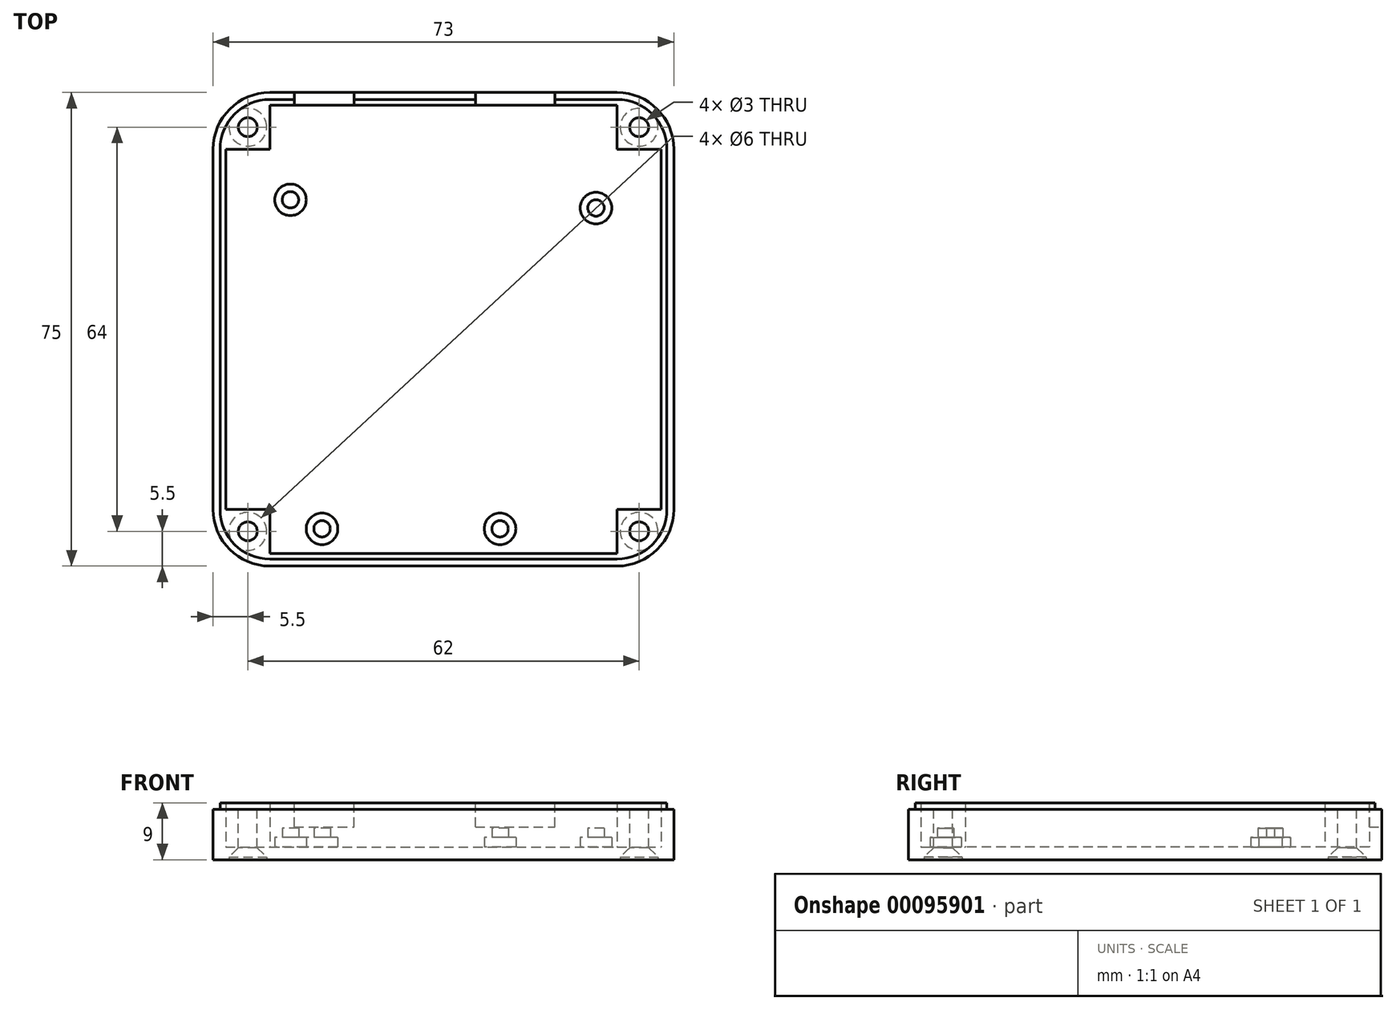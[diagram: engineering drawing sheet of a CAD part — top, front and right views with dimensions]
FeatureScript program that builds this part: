
annotation { "Feature Type Name" : "Feature", "Feature Type Description" : "" }
export const myFeature = defineFeature(function(context is Context, id is Id, definition is map)
    precondition{}
    {
        {
            var Q0;
            Q0=qCreatedBy(makeId("Top.planeOp"),FACE);
            var sketch = newSketch(context, id + "F0", { "sketchPlane" : qUnion([Q0])});
            skLineSegment(sketch, "E0.bottom", {"start": v(-27.5, 38.5) * mm, "end": v(27.5, 38.5) * mm});
            skLineSegment(sketch, "E0.top", {"start": v(-27.5, -36.5) * mm, "end": v(27.5, -36.5) * mm});
            skLineSegment(sketch, "E0.left", {"start": v(-36.5, 29.5) * mm, "end": v(-36.5, -27.5) * mm});
            skLineSegment(sketch, "E0.right", {"start": v(36.5, 29.5) * mm, "end": v(36.5, -27.5) * mm});
            skPoint(sketch, "E1.visualSharp", {"position": v(-36.5, 38.5) * mm});
            skArc(sketch, "E1.filletArc", {"start": v(-27.5, 38.5) * mm, "mid": v(-33.86, 35.86) * mm, "end": v(-36.5, 29.5) * mm});
            skPoint(sketch, "E2.visualSharp", {"position": v(36.5, 38.5) * mm});
            skArc(sketch, "E2.filletArc", {"start": v(36.5, 29.5) * mm, "mid": v(33.86, 35.86) * mm, "end": v(27.5, 38.5) * mm});
            skPoint(sketch, "E3.visualSharp", {"position": v(36.5, -36.5) * mm});
            skArc(sketch, "E3.filletArc", {"start": v(27.5, -36.5) * mm, "mid": v(33.86, -33.86) * mm, "end": v(36.5, -27.5) * mm});
            skPoint(sketch, "E4.visualSharp", {"position": v(-36.5, -36.5) * mm});
            skArc(sketch, "E4.filletArc", {"start": v(-36.5, -27.5) * mm, "mid": v(-33.86, -33.86) * mm, "end": v(-27.5, -36.5) * mm});
            skSolve(sketch);
        }
        {
            var Q0;
            Q0=qSketchRegion(id+"F0",true);
            extrude(context, id + "F1", {"entities" : qUnion([Q0]), "depth" : 2 * mm});
        }
        {
            var Q0;
            Q0=makeQuery(id+"F1.opExtrude","CAP_FACE",FACE,{"disambiguationData":[OSD([sQuery(id+"F0.wireOp",EDGE,"E0.bottom"),sQuery(id+"F0.wireOp",EDGE,"E0.top"),sQuery(id+"F0.wireOp",EDGE,"E0.left"),sQuery(id+"F0.wireOp",EDGE,"E0.right")])],"isStart":false});
            var sketch = newSketch(context, id + "F2", { "sketchPlane" : qUnion([Q0])});
            skCircle(sketch, "E5", {"center": v(-19.24, -30.6) * mm, "radius": 2.5 * mm});
            skCircle(sketch, "E6", {"center": v(8.96, -30.6) * mm, "radius": 2.5 * mm});
            skCircle(sketch, "E7", {"center": v(24.16, 20.2) * mm, "radius": 2.5 * mm});
            skCircle(sketch, "E8", {"center": v(-24.24, 21.5) * mm, "radius": 2.5 * mm});
            skSolve(sketch);
        }
        {
            var Q0;
            Q0=qSketchRegion(id+"F2",true);
            extrude(context, id + "F3", {"entities" : qUnion([Q0]), "operationType" : NewBodyOperationType.ADD, "depth" : 1.5 * mm});
        }
        {
            var Q0;
            Q0=makeQuery(id+"F3.opExtrude","CAP_FACE",FACE,{"disambiguationData":[OSD([sQuery(id+"F2.wireOp",EDGE,"E8")])],"isStart":false});
            var sketch = newSketch(context, id + "F4", { "sketchPlane" : qUnion([Q0])});
            skCircle(sketch, "E9", {"center": v(-19.24, -30.6) * mm, "radius": 1.3 * mm});
            skCircle(sketch, "E10", {"center": v(8.96, -30.6) * mm, "radius": 1.3 * mm});
            skCircle(sketch, "E11", {"center": v(24.16, 20.2) * mm, "radius": 1.3 * mm});
            skCircle(sketch, "E12", {"center": v(-24.24, 21.5) * mm, "radius": 1.3 * mm});
            skSolve(sketch);
        }
        {
            var Q0;
            Q0=qSketchRegion(id+"F4",true);
            extrude(context, id + "F5", {"entities" : qUnion([Q0]), "operationType" : NewBodyOperationType.ADD, "depth" : 1.5 * mm});
        }
        {
            var Q0;
            Q0=makeQuery(id+"F1.opExtrude","CAP_FACE",FACE,{"disambiguationData":[OSD([sQuery(id+"F0.wireOp",EDGE,"E0.bottom"),sQuery(id+"F0.wireOp",EDGE,"E0.top"),sQuery(id+"F0.wireOp",EDGE,"E0.left"),sQuery(id+"F0.wireOp",EDGE,"E0.right"),sQuery(id+"F0.wireOp",EDGE,"E1.filletArc"),sQuery(id+"F0.wireOp",EDGE,"E2.filletArc"),sQuery(id+"F0.wireOp",EDGE,"E3.filletArc"),sQuery(id+"F0.wireOp",EDGE,"E4.filletArc")])],"isStart":false});
            var sketch = newSketch(context, id + "F6", { "sketchPlane" : qUnion([Q0])});
            skLineSegment(sketch, "E13.bottom", {"start": v(-27.5, 38.5) * mm, "end": v(27.5, 38.5) * mm});
            skLineSegment(sketch, "E13.top", {"start": v(-27.5, -36.5) * mm, "end": v(27.5, -36.5) * mm});
            skLineSegment(sketch, "E13.left", {"start": v(-36.5, 29.5) * mm, "end": v(-36.5, -27.5) * mm});
            skLineSegment(sketch, "E13.right", {"start": v(36.5, 29.5) * mm, "end": v(36.5, -27.5) * mm});
            skPoint(sketch, "E14.visualSharp", {"position": v(-36.5, 38.5) * mm});
            skArc(sketch, "E14.filletArc", {"start": v(-27.5, 38.5) * mm, "mid": v(-33.86, 35.86) * mm, "end": v(-36.5, 29.5) * mm});
            skPoint(sketch, "E15.visualSharp", {"position": v(36.5, 38.5) * mm});
            skArc(sketch, "E15.filletArc", {"start": v(36.5, 29.5) * mm, "mid": v(33.86, 35.86) * mm, "end": v(27.5, 38.5) * mm});
            skPoint(sketch, "E16.visualSharp", {"position": v(36.5, -36.5) * mm});
            skArc(sketch, "E16.filletArc", {"start": v(27.5, -36.5) * mm, "mid": v(33.86, -33.86) * mm, "end": v(36.5, -27.5) * mm});
            skPoint(sketch, "E17.visualSharp", {"position": v(-36.5, -36.5) * mm});
            skArc(sketch, "E17.filletArc", {"start": v(-36.5, -27.5) * mm, "mid": v(-33.86, -33.86) * mm, "end": v(-27.5, -36.5) * mm});
            skLineSegment(sketch, "E18", {"start": v(-27.5, 36.5) * mm, "end": v(27.5, 36.5) * mm});
            skLineSegment(sketch, "E19", {"start": v(-34.5, 29.5) * mm, "end": v(-34.5, -27.5) * mm});
            skLineSegment(sketch, "E20", {"start": v(-27.5, -34.5) * mm, "end": v(27.5, -34.5) * mm});
            skLineSegment(sketch, "E21", {"start": v(34.5, 29.5) * mm, "end": v(34.5, -27.5) * mm});
            skLineSegment(sketch, "E22", {"start": v(-34.5, 29.5) * mm, "end": v(-27.5, 29.5) * mm});
            skLineSegment(sketch, "E23", {"start": v(-27.5, 36.5) * mm, "end": v(-27.5, 29.5) * mm});
            skLineSegment(sketch, "E24", {"start": v(27.5, 36.5) * mm, "end": v(27.5, 29.5) * mm});
            skLineSegment(sketch, "E25", {"start": v(27.5, 29.5) * mm, "end": v(34.5, 29.5) * mm});
            skLineSegment(sketch, "E26", {"start": v(-34.5, -27.5) * mm, "end": v(-27.5, -27.5) * mm});
            skLineSegment(sketch, "E27", {"start": v(-27.5, -34.5) * mm, "end": v(-27.5, -27.5) * mm});
            skLineSegment(sketch, "E28", {"start": v(27.5, -34.5) * mm, "end": v(27.5, -27.5) * mm});
            skLineSegment(sketch, "E29", {"start": v(27.5, -27.5) * mm, "end": v(34.5, -27.5) * mm});
            skSolve(sketch);
        }
        {
            var Q0;
            Q0=qSketchRegion(id+"F6",true);
            extrude(context, id + "F7", {"entities" : qUnion([Q0]), "operationType" : NewBodyOperationType.ADD, "depth" : 7 * mm});
        }
        {
            var Q0;
            Q0=makeQuery(id+"F7.opExtrude","CAP_FACE",FACE,{"disambiguationData":[OSD([sQuery(id+"F6.wireOp",EDGE,"E13.bottom"),sQuery(id+"F6.wireOp",EDGE,"E13.top"),sQuery(id+"F6.wireOp",EDGE,"E13.left"),sQuery(id+"F6.wireOp",EDGE,"E13.right"),sQuery(id+"F6.wireOp",EDGE,"E14.filletArc"),sQuery(id+"F6.wireOp",EDGE,"E15.filletArc"),sQuery(id+"F6.wireOp",EDGE,"E16.filletArc"),sQuery(id+"F6.wireOp",EDGE,"E17.filletArc"),sQuery(id+"F6.wireOp",EDGE,"E18"),sQuery(id+"F6.wireOp",EDGE,"E19"),sQuery(id+"F6.wireOp",EDGE,"E20"),sQuery(id+"F6.wireOp",EDGE,"E21"),sQuery(id+"F6.wireOp",EDGE,"E22"),sQuery(id+"F6.wireOp",EDGE,"E23"),sQuery(id+"F6.wireOp",EDGE,"E24"),sQuery(id+"F6.wireOp",EDGE,"E25"),sQuery(id+"F6.wireOp",EDGE,"E26"),sQuery(id+"F6.wireOp",EDGE,"E27"),sQuery(id+"F6.wireOp",EDGE,"E28"),sQuery(id+"F6.wireOp",EDGE,"E29")])],"isStart":false});
            var sketch = newSketch(context, id + "F8", { "sketchPlane" : qUnion([Q0])});
            skCircle(sketch, "E30", {"center": v(-31, 33) * mm, "radius": 1.5 * mm});
            skCircle(sketch, "E31", {"center": v(31, 33) * mm, "radius": 1.5 * mm});
            skCircle(sketch, "E32", {"center": v(-31, -31) * mm, "radius": 1.5 * mm});
            skCircle(sketch, "E33", {"center": v(31, -31) * mm, "radius": 1.5 * mm});
            skSolve(sketch);
        }
        {
            var Q0;
            Q0=qSketchRegion(id+"F8",true);
            extrude(context, id + "F9", {"entities" : qUnion([Q0]), "operationType" : NewBodyOperationType.REMOVE, "oppositeDirection" : true, "depth" : 10 * mm});
        }
        {
            var Q0;
            Q0=makeQuery(id+"F7.opExtrude","CAP_FACE",FACE,{"disambiguationData":[OSD([sQuery(id+"F6.wireOp",EDGE,"E13.bottom"),sQuery(id+"F6.wireOp",EDGE,"E13.top"),sQuery(id+"F6.wireOp",EDGE,"E13.left"),sQuery(id+"F6.wireOp",EDGE,"E13.right"),sQuery(id+"F6.wireOp",EDGE,"E14.filletArc"),sQuery(id+"F6.wireOp",EDGE,"E15.filletArc"),sQuery(id+"F6.wireOp",EDGE,"E16.filletArc"),sQuery(id+"F6.wireOp",EDGE,"E17.filletArc"),sQuery(id+"F6.wireOp",EDGE,"E18"),sQuery(id+"F6.wireOp",EDGE,"E19"),sQuery(id+"F6.wireOp",EDGE,"E20"),sQuery(id+"F6.wireOp",EDGE,"E21"),sQuery(id+"F6.wireOp",EDGE,"E22"),sQuery(id+"F6.wireOp",EDGE,"E23"),sQuery(id+"F6.wireOp",EDGE,"E24"),sQuery(id+"F6.wireOp",EDGE,"E25"),sQuery(id+"F6.wireOp",EDGE,"E26"),sQuery(id+"F6.wireOp",EDGE,"E27"),sQuery(id+"F6.wireOp",EDGE,"E28"),sQuery(id+"F6.wireOp",EDGE,"E29")])],"isStart":false});
            var sketch = newSketch(context, id + "F10", { "sketchPlane" : qUnion([Q0])});
            skLineSegment(sketch, "E34.bottom", {"start": v(17.66, 36.5) * mm, "end": v(5.06, 36.5) * mm});
            skLineSegment(sketch, "E34.top", {"start": v(17.66, 38.5) * mm, "end": v(5.06, 38.5) * mm});
            skLineSegment(sketch, "E34.left", {"start": v(17.66, 36.5) * mm, "end": v(17.66, 38.5) * mm});
            skLineSegment(sketch, "E34.right", {"start": v(5.06, 36.5) * mm, "end": v(5.06, 38.5) * mm});
            skLineSegment(sketch, "E35.bottom", {"start": v(-14.14, 36.5) * mm, "end": v(-23.64, 36.5) * mm});
            skLineSegment(sketch, "E35.top", {"start": v(-14.14, 38.5) * mm, "end": v(-23.64, 38.5) * mm});
            skLineSegment(sketch, "E35.left", {"start": v(-14.14, 36.5) * mm, "end": v(-14.14, 38.5) * mm});
            skLineSegment(sketch, "E35.right", {"start": v(-23.64, 36.5) * mm, "end": v(-23.64, 38.5) * mm});
            skSolve(sketch);
        }
        {
            var Q0;
            Q0=qSketchRegion(id+"F10",true);
            extrude(context, id + "F11", {"entities" : qUnion([Q0]), "operationType" : NewBodyOperationType.REMOVE, "oppositeDirection" : true, "depth" : 3.8 * mm});
        }
        {
            var Q0;
            Q0=makeQuery(id+"F1.opExtrude","CAP_FACE",FACE,{"disambiguationData":[OSD([sQuery(id+"F0.wireOp",EDGE,"E0.bottom"),sQuery(id+"F0.wireOp",EDGE,"E0.top"),sQuery(id+"F0.wireOp",EDGE,"E0.left"),sQuery(id+"F0.wireOp",EDGE,"E0.right"),sQuery(id+"F0.wireOp",EDGE,"E1.filletArc"),sQuery(id+"F0.wireOp",EDGE,"E2.filletArc"),sQuery(id+"F0.wireOp",EDGE,"E3.filletArc"),sQuery(id+"F0.wireOp",EDGE,"E4.filletArc")])],"isStart":true});
            var sketch = newSketch(context, id + "F12", { "sketchPlane" : qUnion([Q0])});
            skCircle(sketch, "E36", {"center": v(31, -33) * mm, "radius": 3 * mm});
            skCircle(sketch, "E37", {"center": v(-31, -33) * mm, "radius": 3 * mm});
            skCircle(sketch, "E38", {"center": v(-31, 31) * mm, "radius": 3 * mm});
            skCircle(sketch, "E39", {"center": v(31, 31) * mm, "radius": 3 * mm});
            skSolve(sketch);
        }
        {
            var Q0;
            Q0=qSketchRegion(id+"F12",true);
            extrude(context, id + "F13", {"entities" : qUnion([Q0]), "operationType" : NewBodyOperationType.REMOVE, "oppositeDirection" : true, "depth" : .4 * mm});
        }
        {
            var Q0;
            Q0=makeQuery(id+"F13.boolean.opBoolean","INTERSECT",EDGE,{"derivedFrom":[makeQuery(id+"F9.boolean.opBoolean","COPY",FACE,{"derivedFrom":makeQuery(id+"F9.opExtrude","SWEPT_FACE",FACE,{"disambiguationData":[OSD([sQuery(id+"F8.wireOp",EDGE,"E31")])]})}),makeQuery(id+"F13.opExtrude","CAP_FACE",FACE,{"disambiguationData":[OSD([sQuery(id+"F12.wireOp",EDGE,"E36")])],"isStart":false})]});
            var Q1;
            Q1=makeQuery(id+"F13.boolean.opBoolean","INTERSECT",EDGE,{"derivedFrom":[makeQuery(id+"F9.boolean.opBoolean","COPY",FACE,{"derivedFrom":makeQuery(id+"F9.opExtrude","SWEPT_FACE",FACE,{"disambiguationData":[OSD([sQuery(id+"F8.wireOp",EDGE,"E30")])]})}),makeQuery(id+"F13.opExtrude","CAP_FACE",FACE,{"disambiguationData":[OSD([sQuery(id+"F12.wireOp",EDGE,"E37")])],"isStart":false})]});
            var Q2;
            Q2=makeQuery(id+"F13.boolean.opBoolean","INTERSECT",EDGE,{"derivedFrom":[makeQuery(id+"F9.boolean.opBoolean","COPY",FACE,{"derivedFrom":makeQuery(id+"F9.opExtrude","SWEPT_FACE",FACE,{"disambiguationData":[OSD([sQuery(id+"F8.wireOp",EDGE,"E33")])]})}),makeQuery(id+"F13.opExtrude","CAP_FACE",FACE,{"disambiguationData":[OSD([sQuery(id+"F12.wireOp",EDGE,"E39")])],"isStart":false})]});
            var Q3;
            Q3=makeQuery(id+"F13.boolean.opBoolean","INTERSECT",EDGE,{"derivedFrom":[makeQuery(id+"F9.boolean.opBoolean","COPY",FACE,{"derivedFrom":makeQuery(id+"F9.opExtrude","SWEPT_FACE",FACE,{"disambiguationData":[OSD([sQuery(id+"F8.wireOp",EDGE,"E32")])]})}),makeQuery(id+"F13.opExtrude","CAP_FACE",FACE,{"disambiguationData":[OSD([sQuery(id+"F12.wireOp",EDGE,"E38")])],"isStart":false})]});
            chamfer(context, id + "F14", {"entities" : qUnion([Q0, Q1, Q2, Q3]), "width" : 1.5 * mm, "tangentPropagation" : true});
        }
        {
            var Q0;
            {var subQ0=sQuery(id+"F6.wireOp",EDGE,"E13.bottom");var subQ1=sQuery(id+"F6.wireOp",EDGE,"E13.top");var subQ2=sQuery(id+"F6.wireOp",EDGE,"E13.left");var subQ3=sQuery(id+"F6.wireOp",EDGE,"E13.right");var subQ4=sQuery(id+"F6.wireOp",EDGE,"E14.filletArc");var subQ5=sQuery(id+"F6.wireOp",EDGE,"E15.filletArc");var subQ6=sQuery(id+"F6.wireOp",EDGE,"E16.filletArc");var subQ7=sQuery(id+"F6.wireOp",EDGE,"E17.filletArc");var subQ8=sQuery(id+"F6.wireOp",EDGE,"E18");var subQ9=sQuery(id+"F6.wireOp",EDGE,"E19");var subQ10=sQuery(id+"F6.wireOp",EDGE,"E20");var subQ11=sQuery(id+"F6.wireOp",EDGE,"E21");var subQ12=sQuery(id+"F6.wireOp",EDGE,"E22");var subQ13=sQuery(id+"F6.wireOp",EDGE,"E23");var subQ14=sQuery(id+"F6.wireOp",EDGE,"E24");var subQ15=sQuery(id+"F6.wireOp",EDGE,"E25");var subQ16=sQuery(id+"F6.wireOp",EDGE,"E26");var subQ17=sQuery(id+"F6.wireOp",EDGE,"E27");var subQ18=sQuery(id+"F6.wireOp",EDGE,"E28");var subQ19=sQuery(id+"F6.wireOp",EDGE,"E29");Q0=makeQuery(id+"F11.boolean.opBoolean","SPLIT",FACE,{"disambiguationData":[TD([makeQuery(id+"F1.opExtrude","SWEPT_FACE",FACE,{"disambiguationData":[OSD([sQuery(id+"F0.wireOp",EDGE,"E0.top")])]})])],"derivedFrom":makeQuery(id+"F7.opExtrude","CAP_FACE",FACE,{"disambiguationData":[OSD([subQ0,subQ1,subQ2,subQ3,subQ4,subQ5,subQ6,subQ7,subQ8,subQ9,subQ10,subQ11,subQ12,subQ13,subQ14,subQ15,subQ16,subQ17,subQ18,subQ19])],"isStart":false})});}
            var sketch = newSketch(context, id + "F15", { "sketchPlane" : qUnion([Q0])});
            skLineSegment(sketch, "E40.0", {"start": v(-27.5, 38.5) * mm, "end": v(-23.64, 38.5) * mm});
            skArc(sketch, "E40.1", {"start": v(-27.5, 38.5) * mm, "mid": v(-33.86, 35.86) * mm, "end": v(-36.5, 29.5) * mm});
            skLineSegment(sketch, "E40.2", {"start": v(-36.5, 29.5) * mm, "end": v(-36.5, -27.5) * mm});
            skArc(sketch, "E40.3", {"start": v(-36.5, -27.5) * mm, "mid": v(-33.86, -33.86) * mm, "end": v(-27.5, -36.5) * mm});
            skLineSegment(sketch, "E40.4", {"start": v(-27.5, -36.5) * mm, "end": v(27.5, -36.5) * mm});
            skArc(sketch, "E40.5", {"start": v(27.5, -36.5) * mm, "mid": v(33.86, -33.86) * mm, "end": v(36.5, -27.5) * mm});
            skLineSegment(sketch, "E40.6", {"start": v(36.5, 29.5) * mm, "end": v(36.5, -27.5) * mm});
            skArc(sketch, "E40.7", {"start": v(36.5, 29.5) * mm, "mid": v(33.86, 35.86) * mm, "end": v(27.5, 38.5) * mm});
            skLineSegment(sketch, "E40.8", {"start": v(17.66, 38.5) * mm, "end": v(27.5, 38.5) * mm});
            skLineSegment(sketch, "E40.9", {"start": v(-14.14, 38.5) * mm, "end": v(5.06, 38.5) * mm});
            skLineSegment(sketch, "E41.top", {"start": v(-14.14, 37.4) * mm, "end": v(5.06, 37.4) * mm});
            skLineSegment(sketch, "E41.left", {"start": v(-14.14, 38.5) * mm, "end": v(-14.14, 37.4) * mm});
            skLineSegment(sketch, "E41.right", {"start": v(5.06, 38.5) * mm, "end": v(5.06, 37.4) * mm});
            skLineSegment(sketch, "E42", {"start": v(-35.4, 29.5) * mm, "end": v(-35.4, -27.5) * mm});
            skLineSegment(sketch, "E43", {"start": v(35.4, 29.5) * mm, "end": v(35.4, -27.5) * mm});
            skLineSegment(sketch, "E44", {"start": v(-27.5, -35.4) * mm, "end": v(27.5, -35.4) * mm});
            skLineSegment(sketch, "E45", {"start": v(-27.5, 37.4) * mm, "end": v(-23.64, 37.4) * mm});
            skLineSegment(sketch, "E46", {"start": v(-23.64, 37.4) * mm, "end": v(-23.64, 38.5) * mm});
            skArc(sketch, "E47", {"start": v(-27.5, 37.4) * mm, "mid": v(-33.09, 35.09) * mm, "end": v(-35.4, 29.5) * mm});
            skLineSegment(sketch, "E48", {"start": v(27.5, 37.4) * mm, "end": v(17.66, 37.4) * mm});
            skLineSegment(sketch, "E49", {"start": v(17.66, 38.5) * mm, "end": v(17.66, 37.4) * mm});
            skArc(sketch, "E50", {"start": v(35.4, 29.5) * mm, "mid": v(33.09, 35.09) * mm, "end": v(27.5, 37.4) * mm});
            skArc(sketch, "E51", {"start": v(27.5, -35.4) * mm, "mid": v(33.09, -33.09) * mm, "end": v(35.4, -27.5) * mm});
            skArc(sketch, "E52", {"start": v(-35.4, -27.5) * mm, "mid": v(-33.09, -33.09) * mm, "end": v(-27.5, -35.4) * mm});
            skSolve(sketch);
        }
        {
            var Q0;
            Q0=qSketchRegion(id+"F15",true);
            extrude(context, id + "F16", {"entities" : qUnion([Q0]), "operationType" : NewBodyOperationType.REMOVE, "oppositeDirection" : true, "depth" : 1 * mm});
        }
    });
